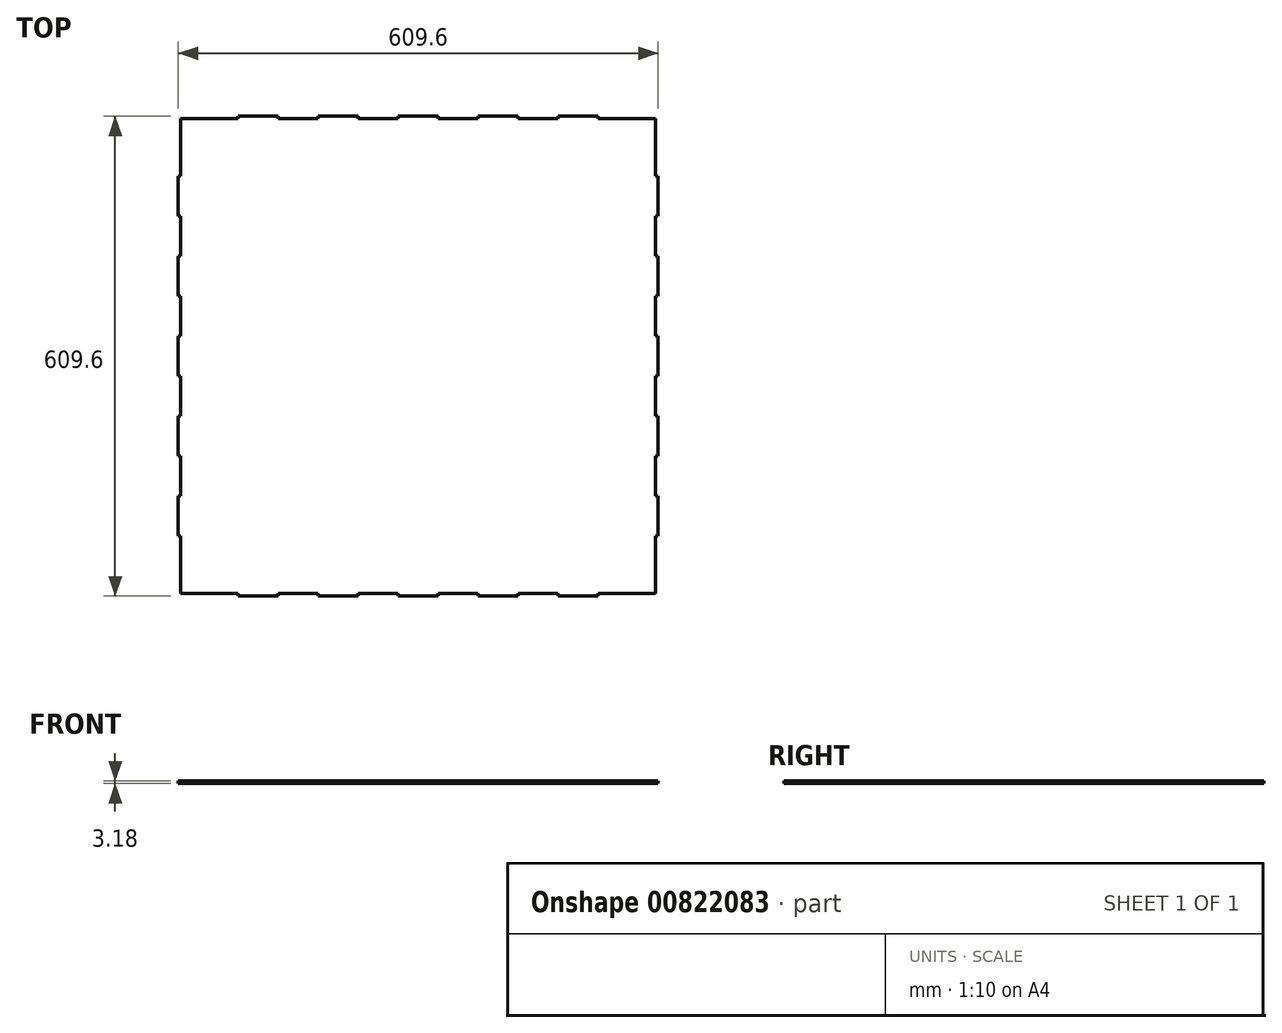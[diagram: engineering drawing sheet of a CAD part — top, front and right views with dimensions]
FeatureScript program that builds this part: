
annotation { "Feature Type Name" : "Feature", "Feature Type Description" : "" }
export const myFeature = defineFeature(function(context is Context, id is Id, definition is map)
    precondition{}
    {
        {
            var Q0;
            Q0=qCreatedBy(makeId("Top.planeOp"),FACE);
            var sketch = newSketch(context, id + "F0", { "sketchPlane" : qUnion([Q0])});
            skLineSegment(sketch, "E0.bottom", {"start": v(-304.8, 304.8) * mm, "end": v(304.8, 304.8) * mm});
            skLineSegment(sketch, "E0.top", {"start": v(-304.8, -304.8) * mm, "end": v(304.8, -304.8) * mm});
            skLineSegment(sketch, "E0.left", {"start": v(-304.8, 304.8) * mm, "end": v(-304.8, -304.8) * mm});
            skLineSegment(sketch, "E0.right", {"start": v(304.8, 304.8) * mm, "end": v(304.8, -304.8) * mm});
            skPoint(sketch, "E0.middle", {"position": v(0, 0) * mm});
            skSolve(sketch);
        }
        {
            var Q0;
            Q0=makeQuery(id+"F0.imprint","IMPRINT",FACE,{"disambiguationData":[TD([[makeQuery(id+"F0.imprint","IMPRINT",EDGE,{"derivedFrom":sQuery(id+"F0.wireOp",EDGE,"E0.bottom")}),-1.0]])]});
            extrude(context, id + "F1", {"entities" : qUnion([Q0]), "depth" : 3.17 * mm, "offsetDistance" : 25.4 * mm});
        }
        {
            var Q0;
            Q0=makeQuery(id+"F1.opExtrude","CAP_FACE",FACE,{"disambiguationData":[OSD([sQuery(id+"F0.wireOp",EDGE,"E0.bottom"),sQuery(id+"F0.wireOp",EDGE,"E0.top"),sQuery(id+"F0.wireOp",EDGE,"E0.left"),sQuery(id+"F0.wireOp",EDGE,"E0.right")])],"isStart":false});
            var sketch = newSketch(context, id + "F2", { "sketchPlane" : qUnion([Q0])});
            skLineSegment(sketch, "E1.bottom", {"start": v(-304.8, -301.63) * mm, "end": v(-228.6, -301.63) * mm});
            skLineSegment(sketch, "E1.top", {"start": v(-304.8, -304.8) * mm, "end": v(-228.6, -304.8) * mm});
            skLineSegment(sketch, "E1.left", {"start": v(-304.8, -301.63) * mm, "end": v(-304.8, -304.8) * mm});
            skLineSegment(sketch, "E1.right", {"start": v(-228.6, -301.63) * mm, "end": v(-228.6, -304.8) * mm});
            skLineSegment(sketch, "E2.1.0", {"start": v(301.63, -304.8) * mm, "end": v(301.63, -228.6) * mm});
            skLineSegment(sketch, "E2.1.1", {"start": v(304.8, -304.8) * mm, "end": v(304.8, -228.6) * mm});
            skLineSegment(sketch, "E2.1.2", {"start": v(301.63, -304.8) * mm, "end": v(304.8, -304.8) * mm});
            skLineSegment(sketch, "E2.1.3", {"start": v(301.63, -228.6) * mm, "end": v(304.8, -228.6) * mm});
            skLineSegment(sketch, "E2.2.0", {"start": v(304.8, 301.63) * mm, "end": v(228.6, 301.63) * mm});
            skLineSegment(sketch, "E2.2.1", {"start": v(304.8, 304.8) * mm, "end": v(228.6, 304.8) * mm});
            skLineSegment(sketch, "E2.2.2", {"start": v(304.8, 301.63) * mm, "end": v(304.8, 304.8) * mm});
            skLineSegment(sketch, "E2.2.3", {"start": v(228.6, 301.63) * mm, "end": v(228.6, 304.8) * mm});
            skLineSegment(sketch, "E2.3.0", {"start": v(-301.63, 304.8) * mm, "end": v(-301.63, 228.6) * mm});
            skLineSegment(sketch, "E2.3.1", {"start": v(-304.8, 304.8) * mm, "end": v(-304.8, 228.6) * mm});
            skLineSegment(sketch, "E2.3.2", {"start": v(-301.63, 304.8) * mm, "end": v(-304.8, 304.8) * mm});
            skLineSegment(sketch, "E2.3.3", {"start": v(-301.63, 228.6) * mm, "end": v(-304.8, 228.6) * mm});
            skPoint(sketch, "E2.center", {"position": v(0, 0) * mm});
            skSolve(sketch);
        }
        {
            var Q0;
            Q0 = qSketchRegion(id + "F2", true);
            extrude(context, id + "F3", {"entities" : qUnion([Q0]), "operationType" : NewBodyOperationType.REMOVE, "oppositeDirection" : true, "depth" : 25.4 * mm, "offsetDistance" : 25.4 * mm});
        }
        {
            var Q0;
            Q0=makeQuery(id+"F1.opExtrude","CAP_FACE",FACE,{"disambiguationData":[OSD([sQuery(id+"F0.wireOp",EDGE,"E0.bottom"),sQuery(id+"F0.wireOp",EDGE,"E0.top"),sQuery(id+"F0.wireOp",EDGE,"E0.left"),sQuery(id+"F0.wireOp",EDGE,"E0.right")])],"isStart":false});
            var sketch = newSketch(context, id + "F4", { "sketchPlane" : qUnion([Q0])});
            skLineSegment(sketch, "E3.bottom", {"start": v(-304.8, -228.6) * mm, "end": v(-301.63, -228.6) * mm});
            skLineSegment(sketch, "E3.top", {"start": v(-304.8, -301.63) * mm, "end": v(-301.63, -301.63) * mm});
            skLineSegment(sketch, "E3.left", {"start": v(-304.8, -228.6) * mm, "end": v(-304.8, -301.63) * mm});
            skLineSegment(sketch, "E3.right", {"start": v(-301.63, -228.6) * mm, "end": v(-301.63, -301.63) * mm});
            skLineSegment(sketch, "E4.1.0", {"start": v(228.6, -304.8) * mm, "end": v(301.63, -304.8) * mm});
            skLineSegment(sketch, "E4.1.1", {"start": v(228.6, -301.63) * mm, "end": v(301.63, -301.63) * mm});
            skLineSegment(sketch, "E4.1.2", {"start": v(228.6, -304.8) * mm, "end": v(228.6, -301.63) * mm});
            skLineSegment(sketch, "E4.1.3", {"start": v(301.63, -304.8) * mm, "end": v(301.63, -301.63) * mm});
            skLineSegment(sketch, "E4.2.0", {"start": v(304.8, 228.6) * mm, "end": v(304.8, 301.63) * mm});
            skLineSegment(sketch, "E4.2.1", {"start": v(301.63, 228.6) * mm, "end": v(301.63, 301.63) * mm});
            skLineSegment(sketch, "E4.2.2", {"start": v(304.8, 228.6) * mm, "end": v(301.63, 228.6) * mm});
            skLineSegment(sketch, "E4.2.3", {"start": v(304.8, 301.63) * mm, "end": v(301.63, 301.63) * mm});
            skLineSegment(sketch, "E4.3.0", {"start": v(-228.6, 304.8) * mm, "end": v(-301.63, 304.8) * mm});
            skLineSegment(sketch, "E4.3.1", {"start": v(-228.6, 301.63) * mm, "end": v(-301.63, 301.63) * mm});
            skLineSegment(sketch, "E4.3.2", {"start": v(-228.6, 304.8) * mm, "end": v(-228.6, 301.63) * mm});
            skLineSegment(sketch, "E4.3.3", {"start": v(-301.63, 304.8) * mm, "end": v(-301.63, 301.63) * mm});
            skPoint(sketch, "E4.center", {"position": v(0, 0) * mm});
            skSolve(sketch);
        }
        {
            var Q0;
            Q0 = qSketchRegion(id + "F4", true);
            extrude(context, id + "F5", {"entities" : qUnion([Q0]), "operationType" : NewBodyOperationType.REMOVE, "oppositeDirection" : true, "depth" : 25.4 * mm, "offsetDistance" : 25.4 * mm});
        }
        {
            var Q0;
            Q0=makeQuery(id+"F1.opExtrude","CAP_FACE",FACE,{"disambiguationData":[OSD([sQuery(id+"F0.wireOp",EDGE,"E0.bottom"),sQuery(id+"F0.wireOp",EDGE,"E0.top"),sQuery(id+"F0.wireOp",EDGE,"E0.left"),sQuery(id+"F0.wireOp",EDGE,"E0.right")])],"isStart":false});
            var sketch = newSketch(context, id + "F6", { "sketchPlane" : qUnion([Q0])});
            skLineSegment(sketch, "E5.bottom", {"start": v(-177.8, -304.8) * mm, "end": v(-127, -304.8) * mm});
            skLineSegment(sketch, "E5.top", {"start": v(-177.8, -301.63) * mm, "end": v(-127, -301.63) * mm});
            skLineSegment(sketch, "E5.left", {"start": v(-177.8, -304.8) * mm, "end": v(-177.8, -301.63) * mm});
            skLineSegment(sketch, "E5.right", {"start": v(-127, -304.8) * mm, "end": v(-127, -301.63) * mm});
            skLineSegment(sketch, "E6.1.0.0", {"start": v(-76.2, -304.8) * mm, "end": v(-25.4, -304.8) * mm});
            skLineSegment(sketch, "E6.1.0.1", {"start": v(-76.2, -301.63) * mm, "end": v(-25.4, -301.63) * mm});
            skLineSegment(sketch, "E6.1.0.2", {"start": v(-76.2, -304.8) * mm, "end": v(-76.2, -301.63) * mm});
            skLineSegment(sketch, "E6.1.0.3", {"start": v(-25.4, -304.8) * mm, "end": v(-25.4, -301.63) * mm});
            skLineSegment(sketch, "E6.2.0.0", {"start": v(25.4, -304.8) * mm, "end": v(76.2, -304.8) * mm});
            skLineSegment(sketch, "E6.2.0.1", {"start": v(25.4, -301.63) * mm, "end": v(76.2, -301.63) * mm});
            skLineSegment(sketch, "E6.2.0.2", {"start": v(25.4, -304.8) * mm, "end": v(25.4, -301.63) * mm});
            skLineSegment(sketch, "E6.2.0.3", {"start": v(76.2, -304.8) * mm, "end": v(76.2, -301.63) * mm});
            skLineSegment(sketch, "E6.3.0.0", {"start": v(127, -304.8) * mm, "end": v(177.8, -304.8) * mm});
            skLineSegment(sketch, "E6.3.0.1", {"start": v(127, -301.63) * mm, "end": v(177.8, -301.63) * mm});
            skLineSegment(sketch, "E6.3.0.2", {"start": v(127, -304.8) * mm, "end": v(127, -301.63) * mm});
            skLineSegment(sketch, "E6.3.0.3", {"start": v(177.8, -304.8) * mm, "end": v(177.8, -301.63) * mm});
            skLineSegment(sketch, "E6.direction1", {"start": v(-177.8, -304.8) * mm, "end": v(-76.2, -304.8) * mm, "construction": true});
            skLineSegment(sketch, "E7.1.0", {"start": v(301.63, -76.2) * mm, "end": v(301.63, -25.4) * mm});
            skLineSegment(sketch, "E7.1.1", {"start": v(304.8, -76.2) * mm, "end": v(304.8, -25.4) * mm});
            skLineSegment(sketch, "E7.1.2", {"start": v(304.8, 25.4) * mm, "end": v(304.8, 76.2) * mm});
            skLineSegment(sketch, "E7.1.3", {"start": v(301.63, 25.4) * mm, "end": v(301.63, 76.2) * mm});
            skLineSegment(sketch, "E7.1.4", {"start": v(304.8, 127) * mm, "end": v(304.8, 177.8) * mm});
            skLineSegment(sketch, "E7.1.5", {"start": v(304.8, -177.8) * mm, "end": v(304.8, -76.2) * mm, "construction": true});
            skLineSegment(sketch, "E7.1.6", {"start": v(301.63, 127) * mm, "end": v(301.63, 177.8) * mm});
            skLineSegment(sketch, "E7.1.7", {"start": v(301.63, -177.8) * mm, "end": v(301.63, -127) * mm});
            skLineSegment(sketch, "E7.1.8", {"start": v(304.8, -177.8) * mm, "end": v(304.8, -127) * mm});
            skLineSegment(sketch, "E7.1.9", {"start": v(304.8, -25.4) * mm, "end": v(301.63, -25.4) * mm});
            skLineSegment(sketch, "E7.1.10", {"start": v(304.8, 25.4) * mm, "end": v(301.63, 25.4) * mm});
            skLineSegment(sketch, "E7.1.11", {"start": v(304.8, 76.2) * mm, "end": v(301.63, 76.2) * mm});
            skLineSegment(sketch, "E7.1.12", {"start": v(304.8, 127) * mm, "end": v(301.63, 127) * mm});
            skLineSegment(sketch, "E7.1.13", {"start": v(304.8, 177.8) * mm, "end": v(301.63, 177.8) * mm});
            skLineSegment(sketch, "E7.1.14", {"start": v(304.8, -76.2) * mm, "end": v(301.63, -76.2) * mm});
            skLineSegment(sketch, "E7.1.15", {"start": v(304.8, -127) * mm, "end": v(301.63, -127) * mm});
            skLineSegment(sketch, "E7.1.16", {"start": v(304.8, -177.8) * mm, "end": v(301.63, -177.8) * mm});
            skLineSegment(sketch, "E7.2.0", {"start": v(76.2, 301.63) * mm, "end": v(25.4, 301.63) * mm});
            skLineSegment(sketch, "E7.2.1", {"start": v(76.2, 304.8) * mm, "end": v(25.4, 304.8) * mm});
            skLineSegment(sketch, "E7.2.2", {"start": v(-25.4, 304.8) * mm, "end": v(-76.2, 304.8) * mm});
            skLineSegment(sketch, "E7.2.3", {"start": v(-25.4, 301.63) * mm, "end": v(-76.2, 301.63) * mm});
            skLineSegment(sketch, "E7.2.4", {"start": v(-127, 304.8) * mm, "end": v(-177.8, 304.8) * mm});
            skLineSegment(sketch, "E7.2.5", {"start": v(177.8, 304.8) * mm, "end": v(76.2, 304.8) * mm, "construction": true});
            skLineSegment(sketch, "E7.2.6", {"start": v(-127, 301.63) * mm, "end": v(-177.8, 301.63) * mm});
            skLineSegment(sketch, "E7.2.7", {"start": v(177.8, 301.63) * mm, "end": v(127, 301.63) * mm});
            skLineSegment(sketch, "E7.2.8", {"start": v(177.8, 304.8) * mm, "end": v(127, 304.8) * mm});
            skLineSegment(sketch, "E7.2.9", {"start": v(25.4, 304.8) * mm, "end": v(25.4, 301.63) * mm});
            skLineSegment(sketch, "E7.2.10", {"start": v(-25.4, 304.8) * mm, "end": v(-25.4, 301.63) * mm});
            skLineSegment(sketch, "E7.2.11", {"start": v(-76.2, 304.8) * mm, "end": v(-76.2, 301.63) * mm});
            skLineSegment(sketch, "E7.2.12", {"start": v(-127, 304.8) * mm, "end": v(-127, 301.63) * mm});
            skLineSegment(sketch, "E7.2.13", {"start": v(-177.8, 304.8) * mm, "end": v(-177.8, 301.63) * mm});
            skLineSegment(sketch, "E7.2.14", {"start": v(76.2, 304.8) * mm, "end": v(76.2, 301.63) * mm});
            skLineSegment(sketch, "E7.2.15", {"start": v(127, 304.8) * mm, "end": v(127, 301.63) * mm});
            skLineSegment(sketch, "E7.2.16", {"start": v(177.8, 304.8) * mm, "end": v(177.8, 301.63) * mm});
            skLineSegment(sketch, "E7.3.0", {"start": v(-301.63, 76.2) * mm, "end": v(-301.63, 25.4) * mm});
            skLineSegment(sketch, "E7.3.1", {"start": v(-304.8, 76.2) * mm, "end": v(-304.8, 25.4) * mm});
            skLineSegment(sketch, "E7.3.2", {"start": v(-304.8, -25.4) * mm, "end": v(-304.8, -76.2) * mm});
            skLineSegment(sketch, "E7.3.3", {"start": v(-301.63, -25.4) * mm, "end": v(-301.63, -76.2) * mm});
            skLineSegment(sketch, "E7.3.4", {"start": v(-304.8, -127) * mm, "end": v(-304.8, -177.8) * mm});
            skLineSegment(sketch, "E7.3.5", {"start": v(-304.8, 177.8) * mm, "end": v(-304.8, 76.2) * mm, "construction": true});
            skLineSegment(sketch, "E7.3.6", {"start": v(-301.63, -127) * mm, "end": v(-301.63, -177.8) * mm});
            skLineSegment(sketch, "E7.3.7", {"start": v(-301.63, 177.8) * mm, "end": v(-301.63, 127) * mm});
            skLineSegment(sketch, "E7.3.8", {"start": v(-304.8, 177.8) * mm, "end": v(-304.8, 127) * mm});
            skLineSegment(sketch, "E7.3.9", {"start": v(-304.8, 25.4) * mm, "end": v(-301.63, 25.4) * mm});
            skLineSegment(sketch, "E7.3.10", {"start": v(-304.8, -25.4) * mm, "end": v(-301.63, -25.4) * mm});
            skLineSegment(sketch, "E7.3.11", {"start": v(-304.8, -76.2) * mm, "end": v(-301.63, -76.2) * mm});
            skLineSegment(sketch, "E7.3.12", {"start": v(-304.8, -127) * mm, "end": v(-301.63, -127) * mm});
            skLineSegment(sketch, "E7.3.13", {"start": v(-304.8, -177.8) * mm, "end": v(-301.63, -177.8) * mm});
            skLineSegment(sketch, "E7.3.14", {"start": v(-304.8, 76.2) * mm, "end": v(-301.63, 76.2) * mm});
            skLineSegment(sketch, "E7.3.15", {"start": v(-304.8, 127) * mm, "end": v(-301.63, 127) * mm});
            skLineSegment(sketch, "E7.3.16", {"start": v(-304.8, 177.8) * mm, "end": v(-301.63, 177.8) * mm});
            skPoint(sketch, "E7.center", {"position": v(0, 0) * mm});
            skSolve(sketch);
        }
        {
            var Q0;
            Q0 = qSketchRegion(id + "F6", true);
            extrude(context, id + "F7", {"entities" : qUnion([Q0]), "operationType" : NewBodyOperationType.REMOVE, "oppositeDirection" : true, "depth" : 25.4 * mm, "offsetDistance" : 25.4 * mm});
        }
    });
